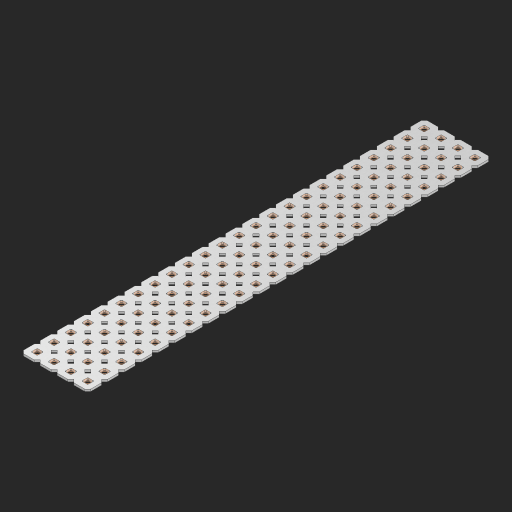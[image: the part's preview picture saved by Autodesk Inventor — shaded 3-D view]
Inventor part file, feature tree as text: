
AUTODESK INVENTOR PART (.ipt)
format: ipt  version: 2023 (Build 270158000, 158)  size: 1,386,496 bytes
history: native  units: in
note: dims shown in document units (in); Inventor stores cm internally (conversion verified against a paired STEP export)
features: other x97, extrude x95, sketch x2, pattern_linear x1
ambient origin geometry x8: Origin, YZ Plane, XZ Plane, XY Plane, X Axis, Y Axis, Z Axis, Center Point
bodies: Solid1 (feature_tree), Body (feature_tree)
feature tree (195):
  pattern_linear  "Rectangular Pattern1"  Spacing1=0.09in  [1 undecoded]
  sketch  "Sketch1"  dims[d1=0.5in]
  sketch  "Sketch2"  dims[d2=0.182in d3=0.09in d4=0.09in d5=0.09in d6=0.09in d7=0.09in d8=0.09in d9=0.09in d10=0.09in d11=0.02in d13=0.0in d14=0.172in d15=0.0625in d16=0.0in d19=0.5in d22=0.5in]
  other  "Srf1"
  other  "Srf126"
  other  "Srf127"
  other  "Srf128"
  other  "Srf129"
  other  "Srf130"
  other  "Srf131"
  other  "Srf250"
  other  "Srf251"
  other  "Srf252"
  other  "Srf253"
  other  "Srf254"
  other  "Srf255"
  other  "Srf256"
  other  "Srf257"
  other  "Srf258"
  other  "Srf259"
  other  "Srf260"
  other  "Srf261"
  other  "Srf262"
  other  "Srf263"
  other  "Srf264"
  other  "Srf265"
  other  "Srf266"
  other  "Srf268"
  other  "Srf269"
  other  "Srf270"
  other  "Srf271"
  other  "Srf272"
  other  "Srf273"
  other  "Srf274"
  other  "Srf275"
  other  "Srf276"
  other  "Srf277"
  other  "Srf278"
  other  "Srf279"
  other  "Srf280"
  other  "Srf281"
  other  "Srf282"
  other  "Srf283"
  other  "Srf284"
  other  "Srf285"
  other  "Srf286"
  other  "Srf287"
  other  "Srf288"
  other  "Srf289"
  other  "Srf290"
  other  "Srf291"
  other  "Srf293"
  other  "Srf294"
  other  "Srf295"
  other  "Srf296"
  other  "Srf297"
  other  "Srf298"
  other  "Srf299"
  other  "Srf300"
  other  "Srf301"
  other  "Srf302"
  other  "Srf303"
  other  "Srf304"
  other  "Srf305"
  other  "Srf306"
  other  "Srf307"
  other  "Srf308"
  other  "Srf309"
  other  "Srf310"
  other  "Srf311"
  other  "Srf312"
  other  "Srf313"
  other  "Srf314"
  other  "Srf315"
  other  "Srf316"
  other  "Srf318"
  other  "Srf319"
  other  "Srf320"
  other  "Srf321"
  other  "Srf322"
  other  "Srf323"
  other  "Srf324"
  other  "Srf325"
  other  "Srf326"
  other  "Srf327"
  other  "Srf328"
  other  "Srf329"
  other  "Srf330"
  other  "Srf331"
  other  "Srf332"
  other  "Srf333"
  other  "Srf334"
  other  "Srf335"
  other  "Srf336"
  other  "Srf337"
  other  "Srf338"
  other  "Srf339"
  other  "Srf340"
  other  "Srf341"
  other  "Circle"
  extrude  "ExtrusionSrf126"  Depth=0.09in
  extrude  "ExtrusionSrf127"  Depth=0.09in
  extrude  "ExtrusionSrf128"  Depth=0.09in
  extrude  "ExtrusionSrf129"  Depth=0.09in
  extrude  "ExtrusionSrf130"  Depth=0.09in
  extrude  "ExtrusionSrf131"  Depth=0.09in
  extrude  "ExtrusionSrf250"  Depth=0.09in
  extrude  "ExtrusionSrf251"  Depth=0.02in
  extrude  "ExtrusionSrf252"  TaperAngle=0.0deg  [1 undecoded]
  extrude  "ExtrusionSrf253"  Depth=0.5in
  extrude  "ExtrusionSrf254"  Depth=0.0625in TaperAngle=0.0deg
  extrude  "ExtrusionSrf255"  Depth=0.5in
  extrude  "ExtrusionSrf256"  Depth=0.5in
  extrude  "ExtrusionSrf257"  [1 undecoded]
  extrude  "ExtrusionSrf258"  [1 undecoded]
  extrude  "ExtrusionSrf259"  [1 undecoded]
  extrude  "ExtrusionSrf260"  [1 undecoded]
  extrude  "ExtrusionSrf261"  [1 undecoded]
  extrude  "ExtrusionSrf262"  [1 undecoded]
  extrude  "ExtrusionSrf263"  [1 undecoded]
  extrude  "ExtrusionSrf264"  [1 undecoded]
  extrude  "ExtrusionSrf265"  [1 undecoded]
  extrude  "ExtrusionSrf266"  [1 undecoded]
  extrude  "ExtrusionSrf268"  [1 undecoded]
  extrude  "ExtrusionSrf269"  [1 undecoded]
  extrude  "ExtrusionSrf270"  [1 undecoded]
  extrude  "ExtrusionSrf271"  [1 undecoded]
  extrude  "ExtrusionSrf272"  [1 undecoded]
  extrude  "ExtrusionSrf273"  [1 undecoded]
  extrude  "ExtrusionSrf274"  [1 undecoded]
  extrude  "ExtrusionSrf275"  [1 undecoded]
  extrude  "ExtrusionSrf276"  [1 undecoded]
  extrude  "ExtrusionSrf277"  [1 undecoded]
  extrude  "ExtrusionSrf278"  [1 undecoded]
  extrude  "ExtrusionSrf279"  [1 undecoded]
  extrude  "ExtrusionSrf280"  [1 undecoded]
  extrude  "ExtrusionSrf281"  [1 undecoded]
  extrude  "ExtrusionSrf282"  [1 undecoded]
  extrude  "ExtrusionSrf283"  [1 undecoded]
  extrude  "ExtrusionSrf284"  [1 undecoded]
  extrude  "ExtrusionSrf285"  [1 undecoded]
  extrude  "ExtrusionSrf286"  [1 undecoded]
  extrude  "ExtrusionSrf287"  [1 undecoded]
  extrude  "ExtrusionSrf288"  [1 undecoded]
  extrude  "ExtrusionSrf289"  [1 undecoded]
  extrude  "ExtrusionSrf290"  [1 undecoded]
  extrude  "ExtrusionSrf291"  [1 undecoded]
  extrude  "ExtrusionSrf293"  [1 undecoded]
  extrude  "ExtrusionSrf294"  [1 undecoded]
  extrude  "ExtrusionSrf295"  [1 undecoded]
  extrude  "ExtrusionSrf296"  [1 undecoded]
  extrude  "ExtrusionSrf297"  [1 undecoded]
  extrude  "ExtrusionSrf298"  [1 undecoded]
  extrude  "ExtrusionSrf299"  [1 undecoded]
  extrude  "ExtrusionSrf300"  [1 undecoded]
  extrude  "ExtrusionSrf301"  [1 undecoded]
  extrude  "ExtrusionSrf302"  [1 undecoded]
  extrude  "ExtrusionSrf303"  [1 undecoded]
  extrude  "ExtrusionSrf304"  [1 undecoded]
  extrude  "ExtrusionSrf305"  [1 undecoded]
  extrude  "ExtrusionSrf306"  [1 undecoded]
  extrude  "ExtrusionSrf307"  [1 undecoded]
  extrude  "ExtrusionSrf308"  [1 undecoded]
  extrude  "ExtrusionSrf309"  [1 undecoded]
  extrude  "ExtrusionSrf310"  [1 undecoded]
  extrude  "ExtrusionSrf311"  [1 undecoded]
  extrude  "ExtrusionSrf312"  [1 undecoded]
  extrude  "ExtrusionSrf313"  [1 undecoded]
  extrude  "ExtrusionSrf314"  [1 undecoded]
  extrude  "ExtrusionSrf315"  [1 undecoded]
  extrude  "ExtrusionSrf316"  [1 undecoded]
  extrude  "ExtrusionSrf318"  [1 undecoded]
  extrude  "ExtrusionSrf319"  [1 undecoded]
  extrude  "ExtrusionSrf320"  [1 undecoded]
  extrude  "ExtrusionSrf321"  [1 undecoded]
  extrude  "ExtrusionSrf322"  [1 undecoded]
  extrude  "ExtrusionSrf323"  [1 undecoded]
  extrude  "ExtrusionSrf324"  [1 undecoded]
  extrude  "ExtrusionSrf325"  [1 undecoded]
  extrude  "ExtrusionSrf326"  [1 undecoded]
  extrude  "ExtrusionSrf327"  [1 undecoded]
  extrude  "ExtrusionSrf328"  [1 undecoded]
  extrude  "ExtrusionSrf329"  [1 undecoded]
  extrude  "ExtrusionSrf330"  [1 undecoded]
  extrude  "ExtrusionSrf331"  [1 undecoded]
  extrude  "ExtrusionSrf332"  [1 undecoded]
  extrude  "ExtrusionSrf333"  [1 undecoded]
  extrude  "ExtrusionSrf334"  [1 undecoded]
  extrude  "ExtrusionSrf335"  [1 undecoded]
  extrude  "ExtrusionSrf336"  [1 undecoded]
  extrude  "ExtrusionSrf337"  [1 undecoded]
  extrude  "ExtrusionSrf338"  [1 undecoded]
  extrude  "ExtrusionSrf339"  [1 undecoded]
  extrude  "ExtrusionSrf340"  [1 undecoded]
  extrude  "ExtrusionSrf341"  [1 undecoded]
note: 84 required parameter values undecoded (feature->parameter linkage not recoverable at this tier; creation-order binding heuristic only, values carry confidence <= 0.55)
